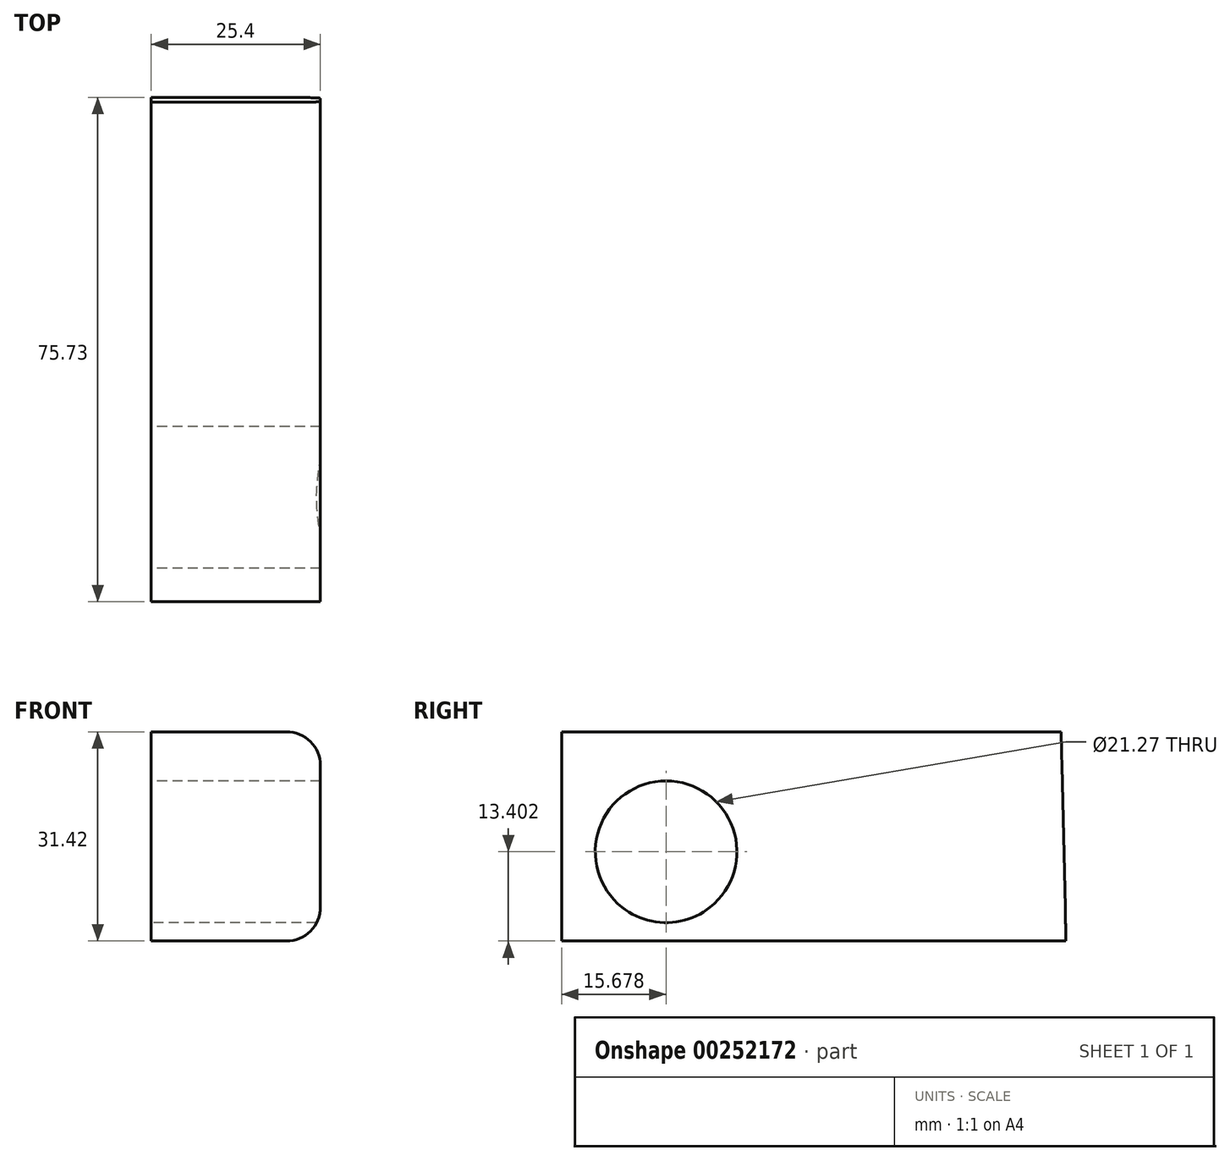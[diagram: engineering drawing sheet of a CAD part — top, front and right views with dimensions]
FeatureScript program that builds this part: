
annotation { "Feature Type Name" : "Feature", "Feature Type Description" : "" }
export const myFeature = defineFeature(function(context is Context, id is Id, definition is map)
    precondition{}
    {
        {
            var Q0;
            Q0=qCreatedBy(makeId("Right.planeOp"),FACE);
            var sketch = newSketch(context, id + "F0", { "sketchPlane" : qUnion([Q0])});
            skLineSegment(sketch, "E0", {"start": v(75, 50.6) * mm, "end": v(0, 50.6) * mm});
            skLineSegment(sketch, "E1", {"start": v(0, 50.6) * mm, "end": v(0, 19.2) * mm});
            skLineSegment(sketch, "E2", {"start": v(0, 19.2) * mm, "end": v(75.73, 19.2) * mm});
            skLineSegment(sketch, "E3", {"start": v(75.73, 19.2) * mm, "end": v(75, 50.6) * mm});
            skSolve(sketch);
        }
        {
            var Q0;
            Q0=makeQuery(id+"F0.imprint","IMPRINT",FACE,{"disambiguationData":[TD([[makeQuery(id+"F0.imprint","IMPRINT",EDGE,{"derivedFrom":sQuery(id+"F0.wireOp",EDGE,"E0")}),1.0]])]});
            var sketch = newSketch(context, id + "F1", { "sketchPlane" : qUnion([Q0])});
            skCircle(sketch, "E4", {"center": v(15.68, 32.6) * mm, "radius": 10.64 * mm});
            skSolve(sketch);
        }
        {
            var Q0;
            Q0=makeQuery(id+"F1.imprint","IMPRINT",FACE,{"disambiguationData":[TD([[makeQuery(id+"F1.imprint","IMPRINT",EDGE,{"derivedFrom":sQuery(id+"F1.wireOp",EDGE,"E4")}),-1.0]])]});
            extrude(context, id + "F2", {"entities" : qUnion([Q0]), "depth" : 25.4 * mm});
        }
        {
            var Q0;
            Q0=makeQuery(id+"F2.opExtrude","CAP_EDGE",EDGE,{"disambiguationData":[OSD([sQuery(id+"F0.wireOp",EDGE,"E0")])],"isStart":false});
            var Q1;
            Q1=makeQuery(id+"F2.opExtrude","CAP_EDGE",EDGE,{"disambiguationData":[OSD([sQuery(id+"F0.wireOp",EDGE,"E2")])],"isStart":false});
            fillet(context, id + "F3", {"entities" : qUnion([Q0, Q1]), "radius" : 5.08 * mm, "tangentPropagation" : true, "allowEdgeOverflow" : false});
        }
    });
